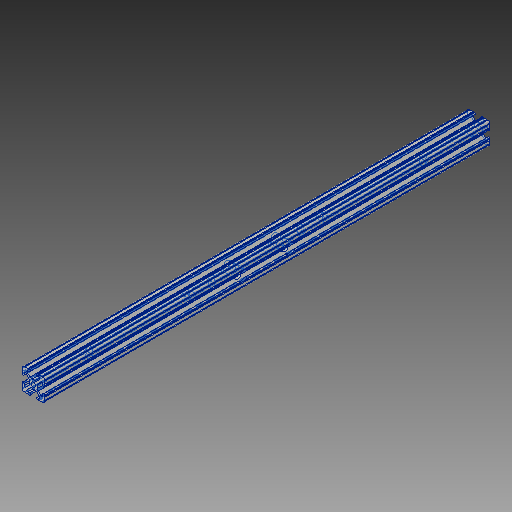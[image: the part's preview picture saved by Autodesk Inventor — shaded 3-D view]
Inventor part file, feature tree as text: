
AUTODESK INVENTOR PART (.ipt)
format: ipt  version: 2019 (Build 230136000, 136)  size: 530,432 bytes
history: native  units: in
note: dims shown in document units (in); Inventor stores cm internally (conversion verified against a paired STEP export)
features: extrude x3, sketch x3, other x1, plane x1, projected_geometry x1
ambient origin geometry x8: Origin, YZ Plane, XZ Plane, XY Plane, X Axis, Y Axis, Z Axis, Center Point
bodies: Solid1 (feature_tree)
feature tree (9):
  other  "Boss-Extrude1"
  extrude  "Extrusion1"  Depth=0.4375in
  plane  "Work Plane1"
  extrude  "Extrusion5"  Depth=0.25in
  extrude  "Extrusion6"  Depth=1.0in TaperAngle=0.0deg
  sketch  "Sketch1"  dims[d0=8.0in d1=0.0in d11=0.4375in]
  projected_geometry  "Projected Loop1"
  sketch  "Sketch6"  dims[d12=2.125in d13=0.25in]
  sketch  "Sketch7"  dims[d14=3.0in d15=1.0in d16=0.0in d17=1.0in d18=0.0in]
